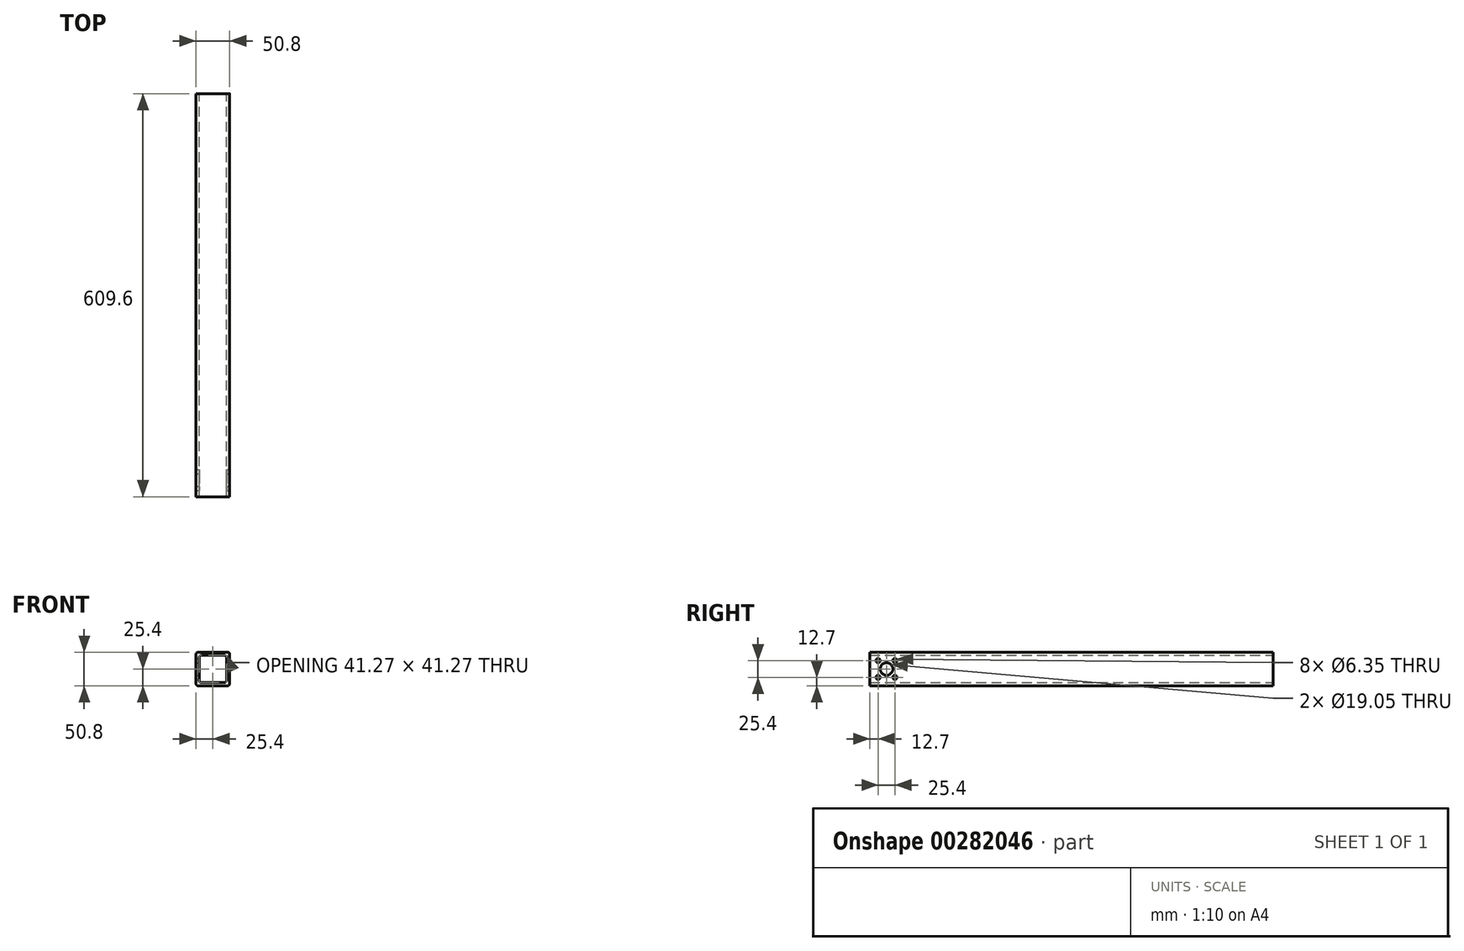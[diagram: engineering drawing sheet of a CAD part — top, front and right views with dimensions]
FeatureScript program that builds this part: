
annotation { "Feature Type Name" : "Feature", "Feature Type Description" : "" }
export const myFeature = defineFeature(function(context is Context, id is Id, definition is map)
    precondition{}
    {
        {
            var Q0;
            Q0=qCreatedBy(makeId("Front.planeOp"),FACE);
            var sketch = newSketch(context, id + "F0", { "sketchPlane" : qUnion([Q0])});
            skLineSegment(sketch, "E0.bottom", {"start": v(22.23, 25.4) * mm, "end": v(-22.23, 25.4) * mm});
            skLineSegment(sketch, "E0.top", {"start": v(22.23, -25.4) * mm, "end": v(-22.23, -25.4) * mm});
            skLineSegment(sketch, "E0.left", {"start": v(25.4, 22.23) * mm, "end": v(25.4, -22.22) * mm});
            skLineSegment(sketch, "E0.right", {"start": v(-25.4, 22.23) * mm, "end": v(-25.4, -22.23) * mm});
            skPoint(sketch, "E0.middle", {"position": v(0, 0) * mm});
            skLineSegment(sketch, "E1.bottom", {"start": v(17.46, 20.64) * mm, "end": v(-17.46, 20.64) * mm});
            skLineSegment(sketch, "E1.top", {"start": v(17.46, -20.64) * mm, "end": v(-17.46, -20.64) * mm});
            skLineSegment(sketch, "E1.left", {"start": v(20.64, 17.46) * mm, "end": v(20.64, -17.46) * mm});
            skLineSegment(sketch, "E1.right", {"start": v(-20.64, 17.46) * mm, "end": v(-20.64, -17.46) * mm});
            skPoint(sketch, "E2.visualSharp", {"position": v(-25.4, 25.4) * mm});
            skArc(sketch, "E2.filletArc", {"start": v(-22.23, 25.4) * mm, "mid": v(-24.47, 24.47) * mm, "end": v(-25.4, 22.23) * mm});
            skPoint(sketch, "E3.visualSharp", {"position": v(-20.64, 20.64) * mm});
            skArc(sketch, "E3.filletArc", {"start": v(-17.46, 20.64) * mm, "mid": v(-19.7, 19.7) * mm, "end": v(-20.64, 17.46) * mm});
            skPoint(sketch, "E4.visualSharp", {"position": v(-20.64, -20.64) * mm});
            skArc(sketch, "E4.filletArc", {"start": v(-20.64, -17.46) * mm, "mid": v(-19.7, -19.7) * mm, "end": v(-17.46, -20.64) * mm});
            skPoint(sketch, "E5.visualSharp", {"position": v(20.64, 20.64) * mm});
            skArc(sketch, "E5.filletArc", {"start": v(20.64, 17.46) * mm, "mid": v(19.7, 19.7) * mm, "end": v(17.46, 20.64) * mm});
            skPoint(sketch, "E6.visualSharp", {"position": v(20.64, -20.64) * mm});
            skArc(sketch, "E6.filletArc", {"start": v(17.46, -20.64) * mm, "mid": v(19.7, -19.7) * mm, "end": v(20.64, -17.46) * mm});
            skPoint(sketch, "E7.visualSharp", {"position": v(-25.4, -25.4) * mm});
            skArc(sketch, "E7.filletArc", {"start": v(-25.4, -22.23) * mm, "mid": v(-24.47, -24.47) * mm, "end": v(-22.23, -25.4) * mm});
            skPoint(sketch, "E8.visualSharp", {"position": v(25.4, 25.4) * mm});
            skArc(sketch, "E8.filletArc", {"start": v(25.4, 22.23) * mm, "mid": v(24.47, 24.47) * mm, "end": v(22.23, 25.4) * mm});
            skPoint(sketch, "E9.visualSharp", {"position": v(25.4, -25.4) * mm});
            skArc(sketch, "E9.filletArc", {"start": v(22.23, -25.4) * mm, "mid": v(24.47, -24.47) * mm, "end": v(25.4, -22.22) * mm});
            skSolve(sketch);
        }
        {
            var Q0;
            Q0 = qSketchRegion(id + "F0", true);
            extrude(context, id + "F1", {"entities" : qUnion([Q0]), "depth" : 609.6 * mm});
        }
        {
            var Q0;
            Q0=makeQuery(id+"F1.opExtrude","SWEPT_FACE",FACE,{"disambiguationData":[OSD([sQuery(id+"F0.wireOp",EDGE,"E0.left")])]});
            var sketch = newSketch(context, id + "F2", { "sketchPlane" : qUnion([Q0])});
            skCircle(sketch, "E10", {"center": v(-584.2, 0) * mm, "radius": 9.53 * mm});
            skLineSegment(sketch, "E11.bottom", {"start": v(-571.5, 12.7) * mm, "end": v(-574.68, 12.7) * mm});
            skLineSegment(sketch, "E11.top", {"start": v(-571.5, -12.7) * mm, "end": v(-574.68, -12.7) * mm});
            skLineSegment(sketch, "E11.left", {"start": v(-571.5, 12.7) * mm, "end": v(-571.5, 9.53) * mm});
            skLineSegment(sketch, "E11.right", {"start": v(-596.9, 12.7) * mm, "end": v(-596.9, 9.53) * mm});
            skCircle(sketch, "E12", {"center": v(-596.9, 12.7) * mm, "radius": 3.18 * mm});
            skCircle(sketch, "E13", {"center": v(-571.5, 12.7) * mm, "radius": 3.18 * mm});
            skCircle(sketch, "E14", {"center": v(-571.5, -12.7) * mm, "radius": 3.18 * mm});
            skCircle(sketch, "E15", {"center": v(-596.9, -12.7) * mm, "radius": 3.18 * mm});
            skLineSegment(sketch, "E16.trimOffspring", {"start": v(-593.73, 12.7) * mm, "end": v(-596.9, 12.7) * mm});
            skLineSegment(sketch, "E17.trimOffspring", {"start": v(-596.9, -9.52) * mm, "end": v(-596.9, -12.7) * mm});
            skLineSegment(sketch, "E18.trimOffspring", {"start": v(-593.73, -12.7) * mm, "end": v(-596.9, -12.7) * mm});
            skLineSegment(sketch, "E19.trimOffspring", {"start": v(-571.5, -9.53) * mm, "end": v(-571.5, -12.7) * mm});
            skSolve(sketch);
        }
        {
            var Q0;
            Q0 = qSketchRegion(id + "F2", true);
            extrude(context, id + "F3", {"entities" : qUnion([Q0]), "operationType" : NewBodyOperationType.REMOVE, "endBound" : BoundingType.THROUGH_ALL, "oppositeDirection" : true, "depth" : 25.4 * mm});
        }
    });
